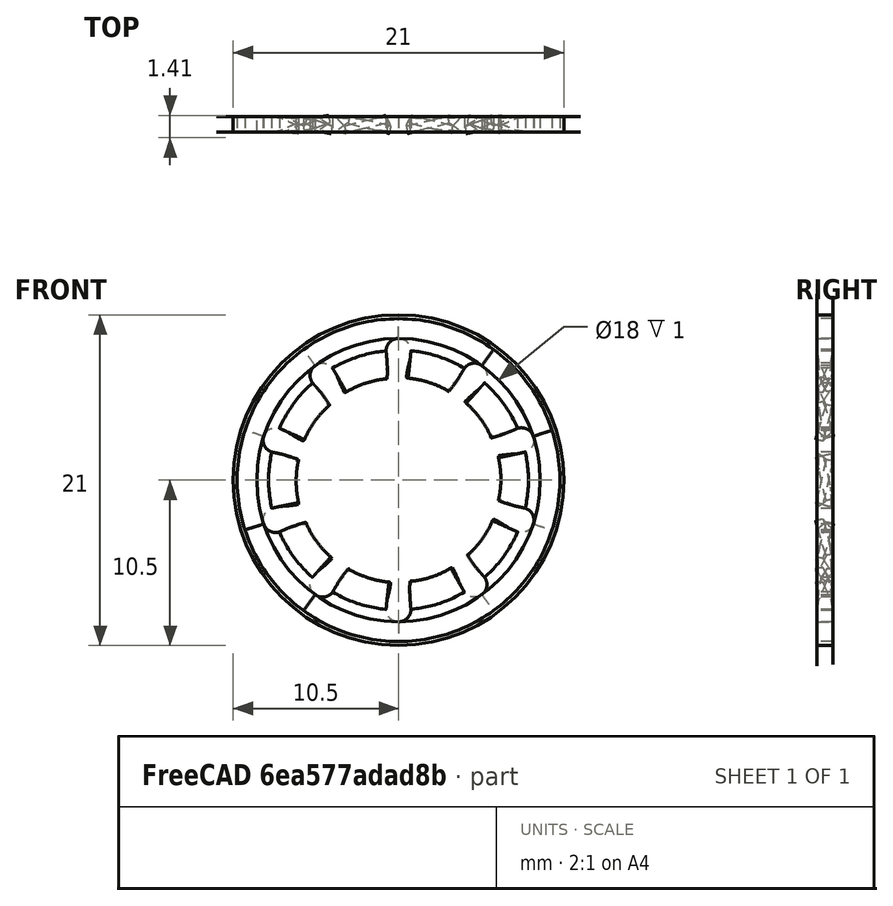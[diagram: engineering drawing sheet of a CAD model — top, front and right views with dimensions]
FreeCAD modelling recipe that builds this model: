
FCSTD DOCUMENT  (FreeCAD 0.19R24267 +99 (Git))
Label: Assembly TR Fastenings Ltd-M12 Internal Toothed Washer DIN 6797J
License: All rights reserved
LicenseURL: http://en.wikipedia.org/wiki/All_rights_reserved
objects: Part::Feature×1, Sketcher::SketchObject×1, PartDesign::Pad×1, PartDesign::Body×1
note: 5 computed .brp shape members not serialized (recipe doc carries the construction recipe); baked Part::Feature solids carry a one-line shape summary decoded from their .brp

FEATURE [Part::Feature] Part__Feature  label="TR Fastenings Ltd-M12"
  Placement = pos=(0,-0.5,0) rot=(0,0,1;0rad)
  shape: bbox 24.07 x 2.092 x 24.81 mm, 140 faces, 10 solids (baked)
FEATURE [Sketcher::SketchObject] Sketch
  FullyConstrained = true
  MapMode = 5
  Placement = pos=(0,0,0) rot=(1,0,0;1.5708rad)
  Support = -> [XZ_Plane]
  sketch-geometry (2):
    g0: Circle CenterX=0 CenterY=0 CenterZ=0 NormalX=0 NormalY=0 NormalZ=1 AngleXU=0 Radius=9
    g1: Circle CenterX=0 CenterY=0 CenterZ=0 NormalX=0 NormalY=0 NormalZ=1 AngleXU=0 Radius=10.5
  constraints (4):
    c: Coincident(g1,g0)
    c: Diameter(g0) = 18
    c: Diameter(g1) = 21
    c: Coincident(g0,g-1)
FEATURE [PartDesign::Pad] Pad
  Direction = (1,1,1)
  Length = 1
  Length2 = 100
  Midplane = true
  Placement = pos=(0,0,0) rot=(1,0,0;1.5708rad)
  Profile = -> Sketch
  Type = 0
FEATURE [PartDesign::Body] Body
  Group = -> [Sketch,Pad]
  Origin = -> Origin
  Tip = -> Pad
